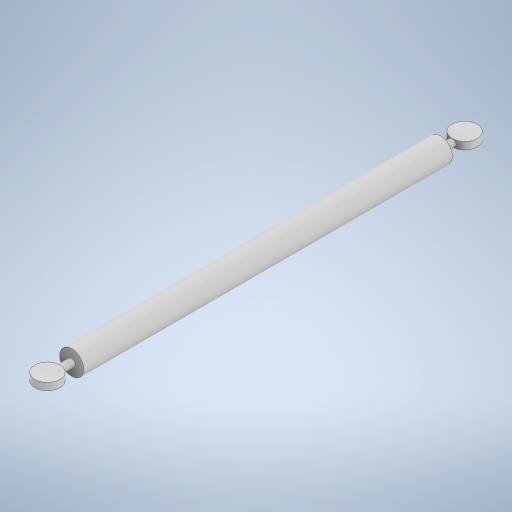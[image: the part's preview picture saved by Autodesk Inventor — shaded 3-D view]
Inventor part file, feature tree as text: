
AUTODESK INVENTOR PART (.ipt)
format: ipt  version: 2023 (Build 270158000, 158)  size: 256,000 bytes
history: native  units: in
note: dims shown in document units (in); Inventor stores cm internally (conversion verified against a paired STEP export)
features: extrude x3, sketch x3, plane x1, mirror x1
ambient origin geometry x8: Origin, YZ Plane, XZ Plane, XY Plane, X Axis, Y Axis, Z Axis, Center Point
bodies: Solid1 (feature_tree)
feature tree (8):
  extrude  "Extrusion1"  Depth=38.0in TaperAngle=0.0deg
  extrude  "Extrusion2"  Depth=0.75in TaperAngle=0.0deg
  extrude  "Extrusion3"  Depth=2.5in
  plane  "Work Plane1"
  mirror  "Mirror1"
  sketch  "Sketch1"  dims[d0=2.5in d1=38.0in d2=0.0in]
  sketch  "Sketch2"  dims[d3=0.75in d4=2.0in d5=0.0in]
  sketch  "Sketch3"  dims[d6=2.6in d7=2.5in d8=0.75in d9=0.0in]
